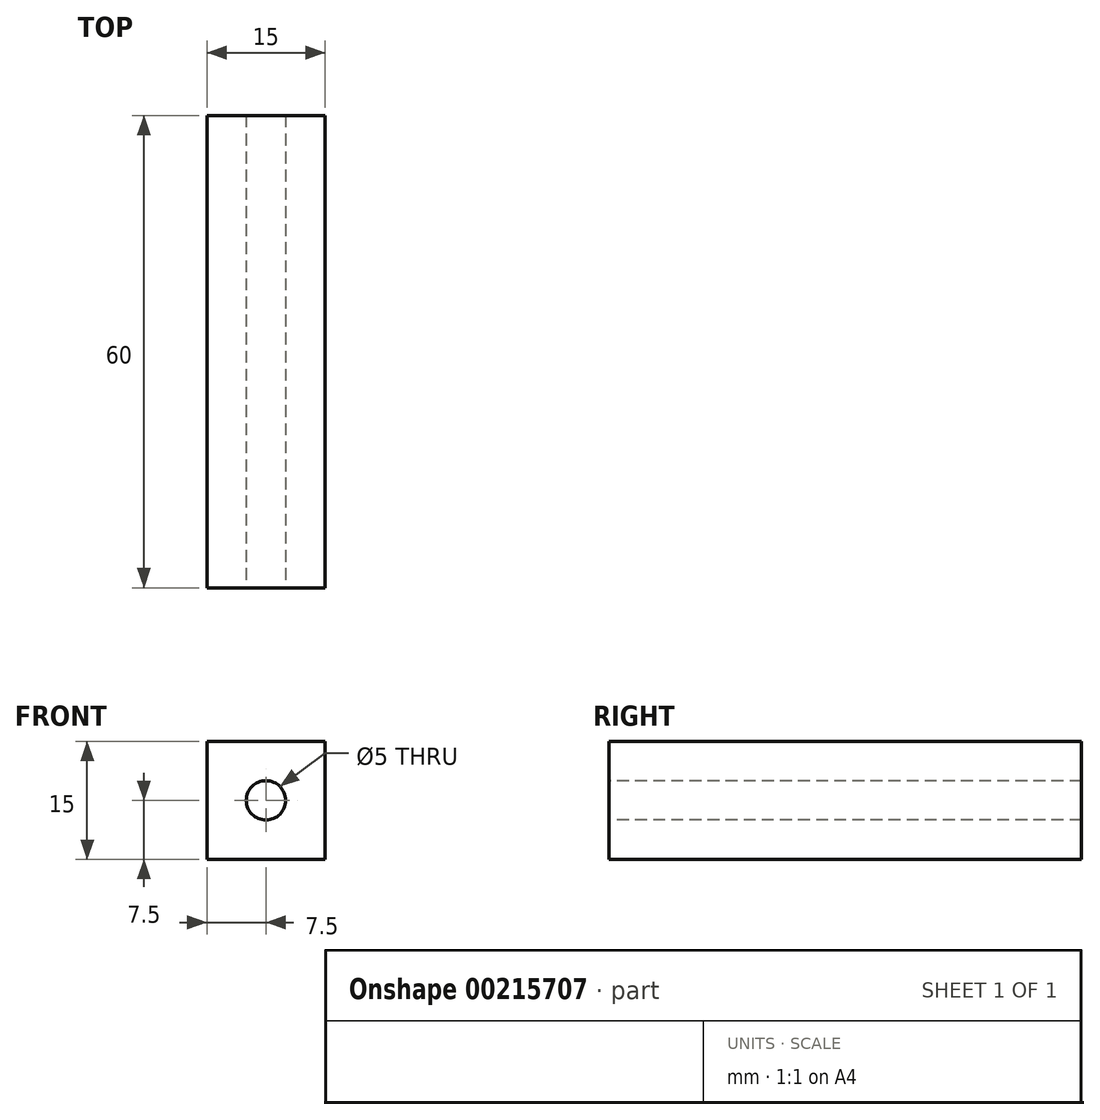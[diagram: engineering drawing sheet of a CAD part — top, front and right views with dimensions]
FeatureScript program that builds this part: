
annotation { "Feature Type Name" : "Feature", "Feature Type Description" : "" }
export const myFeature = defineFeature(function(context is Context, id is Id, definition is map)
    precondition{}
    {
        {
            var Q0;
            Q0=qCreatedBy(makeId("Top.planeOp"),FACE);
            var sketch = newSketch(context, id + "F0", { "sketchPlane" : qUnion([Q0])});
            skLineSegment(sketch, "E0.bottom", {"start": v(0, 0) * mm, "end": v(15, 0) * mm});
            skLineSegment(sketch, "E0.top", {"start": v(0, 60) * mm, "end": v(15, 60) * mm});
            skLineSegment(sketch, "E0.left", {"start": v(0, 0) * mm, "end": v(0, 60) * mm});
            skLineSegment(sketch, "E0.right", {"start": v(15, 0) * mm, "end": v(15, 60) * mm});
            skSolve(sketch);
        }
        {
            var Q0;
            Q0 = qSketchRegion(id + "F0", true);
            extrude(context, id + "F1", {"entities" : qUnion([Q0]), "depth" : 15 * mm});
        }
        {
            var Q0;
            Q0=makeQuery(id+"F1.opExtrude","SWEPT_FACE",FACE,{"disambiguationData":[OSD([sQuery(id+"F0.wireOp",EDGE,"E0.bottom")])]});
            var sketch = newSketch(context, id + "F2", { "sketchPlane" : qUnion([Q0])});
            skCircle(sketch, "E1", {"center": v(7.5, 7.5) * mm, "radius": 2.5 * mm});
            skSolve(sketch);
        }
        {
            var Q0;
            Q0 = qSketchRegion(id + "F2", true);
            extrude(context, id + "F3", {"entities" : qUnion([Q0]), "operationType" : NewBodyOperationType.REMOVE, "endBound" : BoundingType.THROUGH_ALL, "oppositeDirection" : true, "depth" : 25 * mm});
        }
    });
